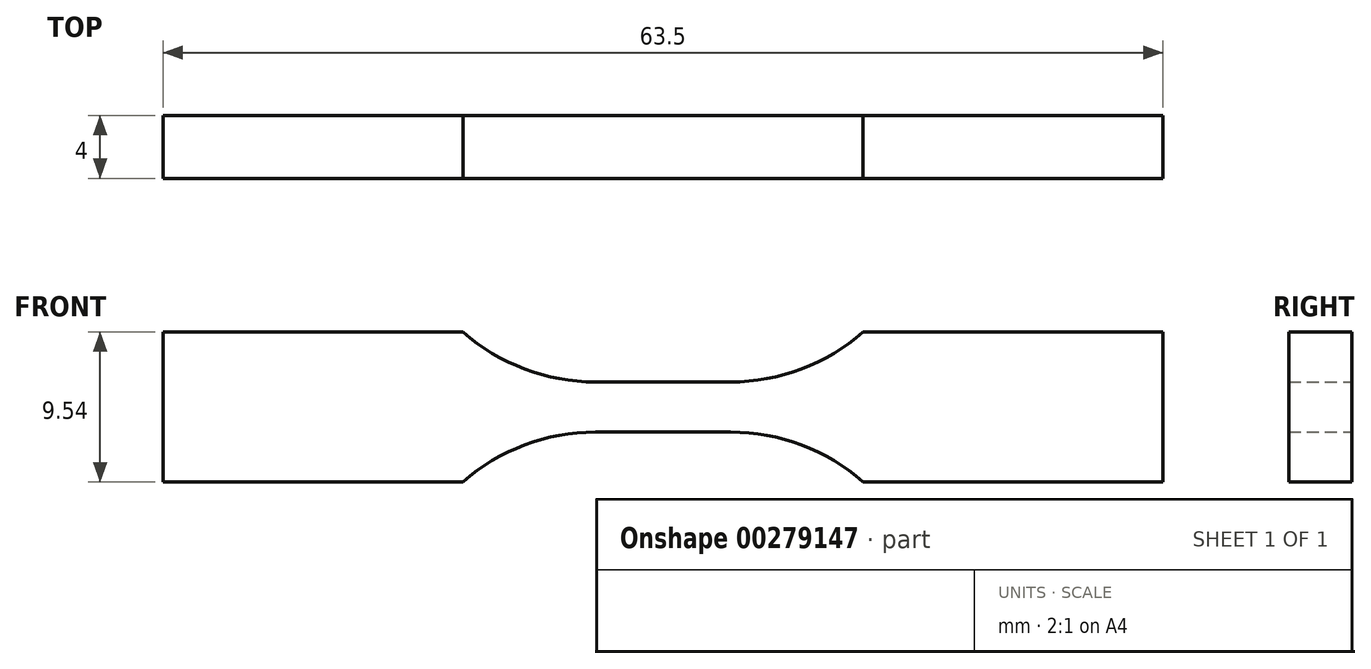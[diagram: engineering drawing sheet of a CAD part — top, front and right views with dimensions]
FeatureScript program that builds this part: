
annotation { "Feature Type Name" : "Feature", "Feature Type Description" : "" }
export const myFeature = defineFeature(function(context is Context, id is Id, definition is map)
    precondition{}
    {
        {
            var Q0;
            Q0=qCreatedBy(makeId("Front.planeOp"),FACE);
            var sketch = newSketch(context, id + "F0", { "sketchPlane" : qUnion([Q0])});
            skLineSegment(sketch, "E0", {"start": v(0, 1.6) * mm, "end": v(4.3, 1.6) * mm});
            skArc(sketch, "E1", {"start": v(4.3, 1.59) * mm, "mid": v(8.79, 2.41) * mm, "end": v(12.7, 4.76) * mm});
            skLineSegment(sketch, "E2", {"start": v(12.7, 4.76) * mm, "end": v(31.75, 4.76) * mm});
            skLineSegment(sketch, "E3.MirrorCS", {"start": v(12.7, -4.76) * mm, "end": v(31.75, -4.76) * mm});
            skLineSegment(sketch, "E4.MirrorCS", {"start": v(0, -1.6) * mm, "end": v(4.3, -1.6) * mm});
            skArc(sketch, "E5.MirrorCS", {"start": v(4.3, -1.59) * mm, "mid": v(8.79, -2.41) * mm, "end": v(12.7, -4.76) * mm});
            skArc(sketch, "E6.MirrorCS", {"start": v(-4.3, -1.59) * mm, "mid": v(-8.79, -2.41) * mm, "end": v(-12.7, -4.76) * mm});
            skLineSegment(sketch, "E7.MirrorCS", {"start": v(0, 1.6) * mm, "end": v(-4.3, 1.6) * mm});
            skArc(sketch, "E8.MirrorCS", {"start": v(-4.3, 1.59) * mm, "mid": v(-8.79, 2.41) * mm, "end": v(-12.7, 4.76) * mm});
            skLineSegment(sketch, "E9.MirrorCS", {"start": v(-12.7, -4.76) * mm, "end": v(-31.75, -4.77) * mm});
            skLineSegment(sketch, "E10.MirrorCS", {"start": v(0, -1.6) * mm, "end": v(-4.3, -1.6) * mm});
            skLineSegment(sketch, "E11.MirrorCS", {"start": v(-12.7, 4.77) * mm, "end": v(-31.75, 4.76) * mm});
            skLineSegment(sketch, "E12", {"start": v(-31.75, 4.76) * mm, "end": v(-31.75, -4.76) * mm});
            skLineSegment(sketch, "E13", {"start": v(31.75, 4.76) * mm, "end": v(31.75, -4.76) * mm});
            skSolve(sketch);
        }
        {
            var Q0;
            Q0=makeQuery(id+"F0.imprint","IMPRINT",FACE,{"disambiguationData":[TD([[makeQuery(id+"F0.imprint","IMPRINT",EDGE,{"derivedFrom":sQuery(id+"F0.wireOp",EDGE,"E0")}),-1.0]])]});
            extrude(context, id + "F1", {"entities" : qUnion([Q0]), "endBound" : BoundingType.SYMMETRIC, "depth" : 4 * mm});
        }
    });
